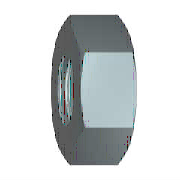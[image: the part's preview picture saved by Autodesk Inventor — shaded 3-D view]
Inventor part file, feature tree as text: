
AUTODESK INVENTOR PART (.ipt)
format: ipt  version: 2020 (Build 240168000, 168)  size: 167,424 bytes
history: native  units: mm (DEFAULTED — no unit token found)
features: sketch x3, chamfer x1, hole x1, other x1, plane x1
ambient origin geometry x7: Origin, YZ Plane, XZ Plane, X Axis, Y Axis, Z Axis, Center Point
bodies: Solid1 (feature_tree), Body (feature_tree)
feature tree (7):
  chamfer  "Chamfer1"  Angle=30.0deg  [1 undecoded]
  hole  "Thread"  [1 undecoded]
  other  "Work Axis1"
  plane  "Work Plane1"
  sketch  "Sketch1"  dims[d0=8.082904mm]
  sketch  "Sketch2"  dims[d1=3.2mm]
  sketch  "Sketch3"  dims[d2=0.0mm d3=30.0deg d4=30.0deg d5=5.9mm d6=5.9mm d7=90.0deg d25=3.242mm d26=6.0mm d27=4.0mm d28=2.0mm d29=14.3117mm d30=8.0mm d31=20.594885mm d8=0.378886mm d9=30.0deg d10=0.378886mm d11=30.0deg d13=0.0mm d14=0.0mm d39=0.0mm d40=0.378886mm d41=0.378886mm d42=0.0mm]
note: 2 required parameter values undecoded (feature->parameter linkage not recoverable at this tier; creation-order binding heuristic only, values carry confidence <= 0.55)
